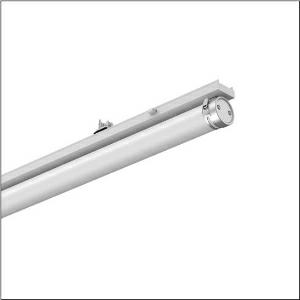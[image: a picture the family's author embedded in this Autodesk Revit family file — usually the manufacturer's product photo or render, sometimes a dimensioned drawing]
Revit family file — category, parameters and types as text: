
# Revit family: monsun_r__31_tube_51ft10nn4a0atr2_f2a8
name_source: partatom
category: Lighting Fixtures
units: mm (PartAtom-declared; Revit-internal decimal feet)

## family parameters
Cut with Voids When Loaded = No
Host = Face
Light Source = No
Part Type = Normal
Room Calculation Point = No
Round Connector Dimension = Use Diameter
Shared = No

## types (1)
- --- (1 x LED, 10000 lm, 58 W, 4000K)
    Apparent Load = 58 VA
    CIE Flux Codes = 42 71 90 91 100
    Color Rendering = 80
    Color Temperature = 4000K
    Default Elevation = 1800 mm
    Description = Monsun® 31 Tube, tubular luminaire, primary optical cover: diffuser, of PMMA, light emission: direct distribution, primary light characteristic: symmetric, LED, rated luminous flux: 10.000lm, luminous efficacy: 172lm/W, light colour: 840, colour temperature: 4000K, control gear: DALI Multilumen, with with 1 terminal, 5-pole, max. 2.5mm², mains connection: 220..240V, AC, 50/60Hz, rated input power: 58W, housing, cylindrical, of PMMA, semi-transparent, matt white, with luminaire and ceiling fastening, V4A, mounting with brackets of stainless steel, length: 1.500mm, diameter: 75mm, end cap, of stainless steel (V4A), protection rating (complete): IP20, protection rating (lamp compartment): IP67/69K, insulation class (complete): insulation class I (protective earthing), certification: CE, UKCA, impact resistance: IK06, permissible operating ambient temperature: -20..+40°C, corresponds to IFS (International Featured Standards) requirements for safety and quality in the food industry, contact your sales advisor before using the luminaires in applications with unclear chemical exposure, large temperature fluctuations or condensation-forming humidity, packaging unit: 1 piece
    Height = 132 mm
    Lamp = 1 x LED
    Lamp Light Flux = 10000 lm
    Lamp Power = 58 W
    Lamp count = 1
    Length = 1500 mm
    Luminous efficacy = 172 lm/W
    Manufacturer = Siteco
    ModVariant = No
    Model = 51FT10NN4A0ATR2
    Mounting Place = Ceiling
    Mounting Type = Pendant
    Number of Poles = 1
    OnlyDefault = Yes
    Power Factor = 1
    Product Name = Monsun® 31 Tube
    Product group = tubular luminaire
    ProductGroupID = 906
    Protection Class = Protection class I
    Protection Degree = IP 20
    RLX_Detail_Level = 1
    RLX_Emergency_Light_Flux = 0 lm
    RLX_Emergency_Type = 0
    RLX_Emergency_Type_DB = No
    RlxData = <blob elided: 32401 chars, md5=2cc00b26>
    Socket = socket
    Standby Power = 0 W
    System Light Flux = 10000 lm
    System Power = 58 W
    Type Comments = individual setting: luminous flux: 100 % | (OFF | OFF | ON | OFF) | 350 mA
    Type Image = l_1242814.jpg
    URL = http://relux.com
    VarID = @adj_164833
    Voltage = 0 V
    Weight = 0.00 kg
    Width = 79 mm

## geometry (parser evidence)
native form markers: Blend x4, Sweep x12
no freeform markers — native parametric forms only
